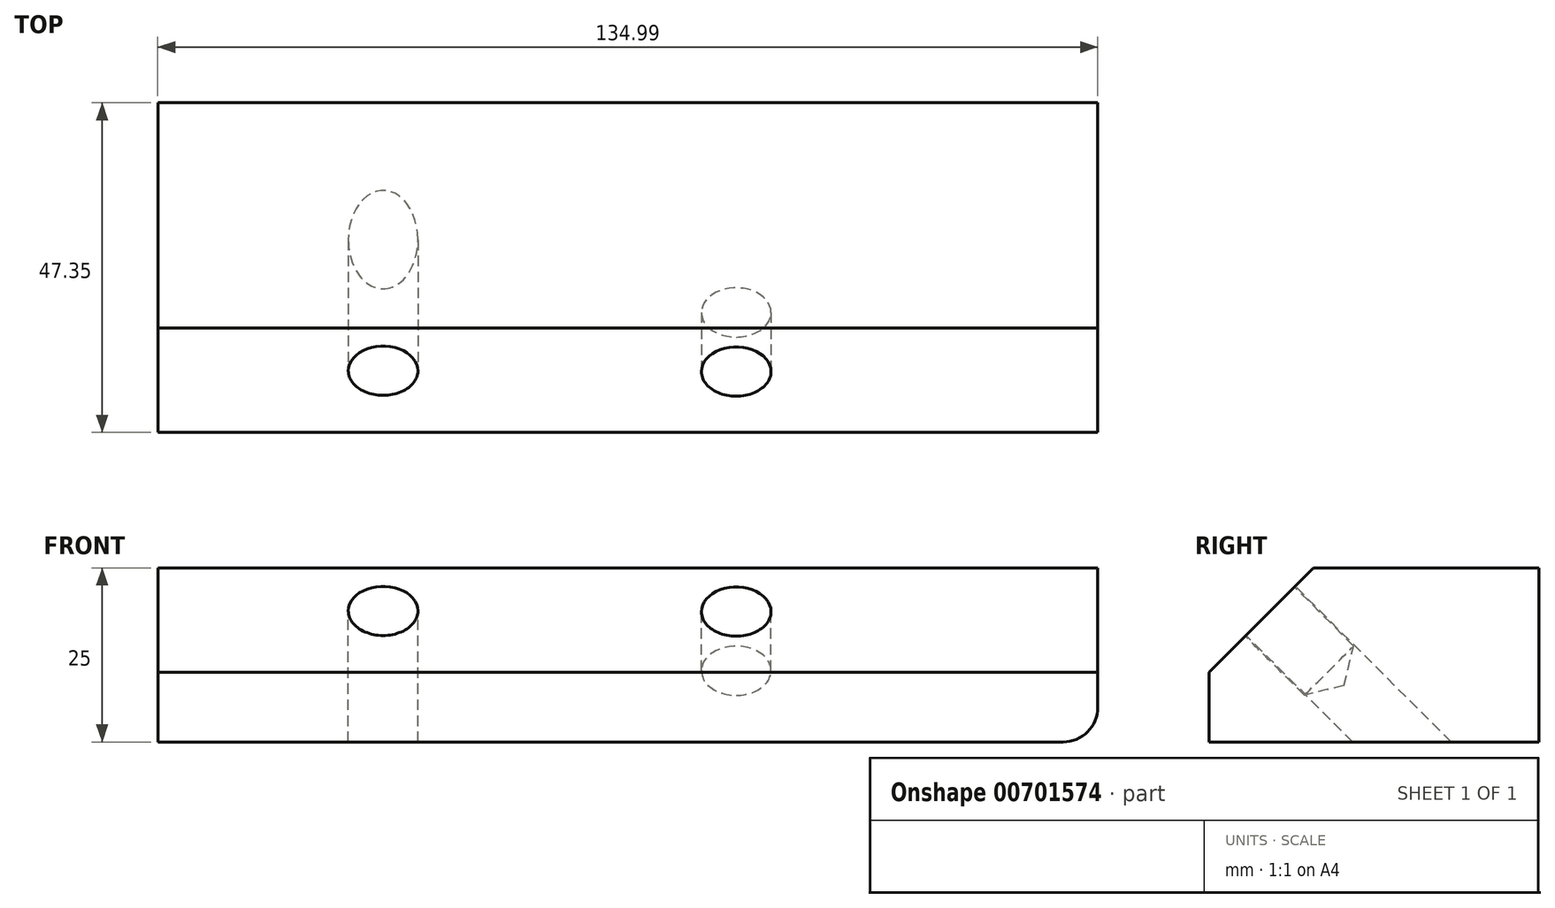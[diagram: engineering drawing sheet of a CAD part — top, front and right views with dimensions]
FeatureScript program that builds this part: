
annotation { "Feature Type Name" : "Feature", "Feature Type Description" : "" }
export const myFeature = defineFeature(function(context is Context, id is Id, definition is map)
    precondition{}
    {
        {
            var Q0;
            Q0=qCreatedBy(makeId("Top.planeOp"),FACE);
            var sketch = newSketch(context, id + "F0", { "sketchPlane" : qUnion([Q0])});
            skLineSegment(sketch, "E0.bottom", {"start": v(-134.99, -47.35) * mm, "end": v(0, -47.35) * mm});
            skLineSegment(sketch, "E0.top", {"start": v(-134.99, 0) * mm, "end": v(0, 0) * mm});
            skLineSegment(sketch, "E0.left", {"start": v(-134.99, -47.35) * mm, "end": v(-134.99, 0) * mm});
            skLineSegment(sketch, "E0.right", {"start": v(0, -47.35) * mm, "end": v(0, 0) * mm});
            skSolve(sketch);
        }
        {
            var Q0;
            Q0 = qSketchRegion(id + "F0", true);
            extrude(context, id + "F1", {"entities" : qUnion([Q0]), "depth" : 25 * mm, "offsetDistance" : 25 * mm});
        }
        {
            var Q0;
            Q0=makeQuery(id+"F1.opExtrude","CAP_EDGE",EDGE,{"disambiguationData":[OSD([sQuery(id+"F0.wireOp",EDGE,"E0.bottom")])],"isStart":false});
            chamfer(context, id + "F2", {"entities" : qUnion([Q0]), "width" : 15 * mm, "tangentPropagation" : true});
        }
        {
            var Q0;
            Q0=makeQuery(id+"F2.opChamfer","BLEND_FACE",FACE,{"disambiguationData":[OSD([sQuery(id+"F0.wireOp",EDGE,"E0.bottom")])]});
            var sketch = newSketch(context, id + "F3", { "sketchPlane" : qUnion([Q0])});
            skPoint(sketch, "E1", {"position": v(-102.63, -13.9) * mm});
            skSolve(sketch);
        }
        {
            var Q0;
            {var subQ0=sQuery(id+"F0.wireOp",EDGE,"E0.bottom");var subQ1=makeQuery(id+"F1.opExtrude","CAP_EDGE",EDGE,{"disambiguationData":[OSD([subQ0])],"isStart":false});Q0=makeQuery(id+"F3.imprint","IMPRINT",FACE,{"disambiguationData":[TD([[makeQuery(id+"F3.imprint","IMPRINT",EDGE,{"derivedFrom":makeQuery(id+"F2.opChamfer","BLEND_EDGE",EDGE,{"blendedFrom":[subQ1,makeQuery(id+"F1.opExtrude","SWEPT_FACE",FACE,{"disambiguationData":[OSD([subQ0])]})],"blendedInto":[makeQuery(id+"F1.opExtrude","SWEPT_FACE",FACE,{"disambiguationData":[OSD([subQ0])]})]})}),-1.0]])]});}
            var sketch = newSketch(context, id + "F4", { "sketchPlane" : qUnion([Q0])});
            skPoint(sketch, "E2", {"position": v(-51.92, -14.06) * mm});
            skSolve(sketch);
        }
        {
            var Q0;
            Q0=sQuery(id+"F3.wireOp",VERTEX,"E1");
            var Q1;
            Q1=makeQuery(id+"F1.opExtrude","SWEPT_BODY",BODY,{"disambiguationData":[OSD([sQuery(id+"F0.wireOp",EDGE,"E0.bottom"),sQuery(id+"F0.wireOp",EDGE,"E0.top"),sQuery(id+"F0.wireOp",EDGE,"E0.left"),sQuery(id+"F0.wireOp",EDGE,"E0.right")])]});
            hole(context, id + "F5", {"style" : HoleStyle.SIMPLE, "endStyle" : HoleEndStyle.THROUGH, "holeDiameter" : 10 * mm, "majorDiameter" : 5 * mm, "isTappedThrough" : true, "tappedDepth" : 12 * mm, "tapClearance" : 3, "locations" : qUnion([Q0]), "scope" : qUnion([Q1])});
        }
        {
            var Q0;
            Q0=sQuery(id+"F4.wireOp",VERTEX,"E2");
            var Q1;
            Q1=makeQuery(id+"F1.opExtrude","SWEPT_BODY",BODY,{"disambiguationData":[OSD([sQuery(id+"F0.wireOp",EDGE,"E0.bottom"),sQuery(id+"F0.wireOp",EDGE,"E0.top"),sQuery(id+"F0.wireOp",EDGE,"E0.left"),sQuery(id+"F0.wireOp",EDGE,"E0.right")])]});
            hole(context, id + "F6", {"style" : HoleStyle.SIMPLE, "endStyle" : HoleEndStyle.BLIND, "holeDiameter" : 10 * mm, "majorDiameter" : 5 * mm, "holeDepth" : 12 * mm, "isTappedThrough" : true, "tappedDepth" : 12 * mm, "tapClearance" : 3, "locations" : qUnion([Q0]), "scope" : qUnion([Q1])});
        }
        {
            var Q0;
            Q0=makeQuery(id+"F1.opExtrude","CAP_EDGE",EDGE,{"disambiguationData":[OSD([sQuery(id+"F0.wireOp",EDGE,"E0.right")])],"isStart":true});
            fillet(context, id + "F7", {"entities" : qUnion([Q0]), "radius" : 5 * mm, "tangentPropagation" : true, "allowEdgeOverflow" : false});
        }
    });
